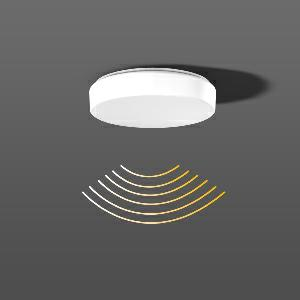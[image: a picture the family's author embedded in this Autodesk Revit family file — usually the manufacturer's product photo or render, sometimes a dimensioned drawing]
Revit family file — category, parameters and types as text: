
# Revit family: flat_polymero_kreis_311950_002_2_19_db8e
name_source: partatom
category: Lighting Fixtures
units: mm (PartAtom-declared; Revit-internal decimal feet)

## family parameters
Cut with Voids When Loaded = No
Host = Face
Light Source = No
Part Type = Normal
Room Calculation Point = No
Round Connector Dimension = Use Diameter
Shared = No

## types (1)
- FLAT POLYMERO KREIS (1 x LED Modul 830, 1200 lm, 3000)
    Apparent Load = 12 VA
    CIE Flux Codes = 42 73 92 87 100
    Color Rendering = 80
    Color Temperature = 3000
    Default Elevation = 1800 mm
    Description = Series: FLAT POLYMERO KREIS
Decorative round surface-mounted luminaire. Base: metal, powder-coated. Diffuser made of plastic (polycarbonate), opal, shockproof. Diffuser fastening: patented push system. Suitable for Ceiling mounting, Wall (surface). With integrated HF movement sensor. Functional parameters of a master luminaire (ceiling height of approx. 2.8 m): HF detector 24 GHz with integrated corridor function. Coverage: approx. 130° radial. Easy adjustment of functions via 3 associated push button switches. Sensitivity/Range: 0.5-5 m radial, adjustable from 10-100%. Time control 1 second to 15 minutes in 8 different levels. Daylight detection with 5 brightness levels and learning mode. Up to 9 slave luminaires can be operated with one master luminaire (max. up to 150 W / 230 W). Suitable for outdoor use to a limited extent only, as it is sensitive to all movements. 
Colour: white
Diameter: 360 mm
Height: 87 mm
Lamp: LED exchangeable
Socket: without socket
Colour temperature: 3000K
Colour rendering index (CRI): 83
System power: 12 W
Rated luminous flux: 1200 lm
Luminous efficiency: 100 lm/W
Control gear: Converter not necessary
Protection class: I
Type of protection: IP 40
    Height = 87 mm
    Lamp = 1 x LED Modul 830
    Lamp Light Flux = 1200 lm
    Lamp count = 1
    Length = 360 mm
    Lifetime = 50000 h
    Luminous efficacy = 100 lm/W
    Manufacturer = RZB
    ModVariant = No
    Model = 311950.002.2.19
    Mounting Place = Ceiling, Wall
    Mounting Type = Surface mounted
    Number of Poles = 1
    OnlyDefault = Yes
    Power Factor = 1
    Product Name = FLAT POLYMERO KREIS
    Product group = Surface mounted ceiling and wall luminaires
    ProductGroupID = 305
    Protection Class = Protection class I
    Protection Degree = IP 40
    RLX_Detail_Level = 1
    RLX_Emergency_Light_Flux = 0 lm
    RLX_Emergency_Type = 0
    RLX_Emergency_Type_DB = No
    RlxData = <blob elided: 65473 chars, md5=18932564>
    Socket = socket
    Standby Power = 0 W
    System Light Flux = 1200 lm
    System Power = 12 W
    Type Comments = Product without accessories
    Type Image = 311599.002.19.jpg
    URL = http://relux.com
    VarID = ---
    Voltage = 230 V
    Voltage Range = 220-240 V
    Weight = 0.00 kg
    Width = 0 mm  [stored 0 ft]

note: [stored X ft] marks values corroborated as IEEE doubles in the binary element streams (Revit-internal decimal feet)

## geometry (parser evidence)
native form markers: Blend x4, Sweep x11
no freeform markers — native parametric forms only
